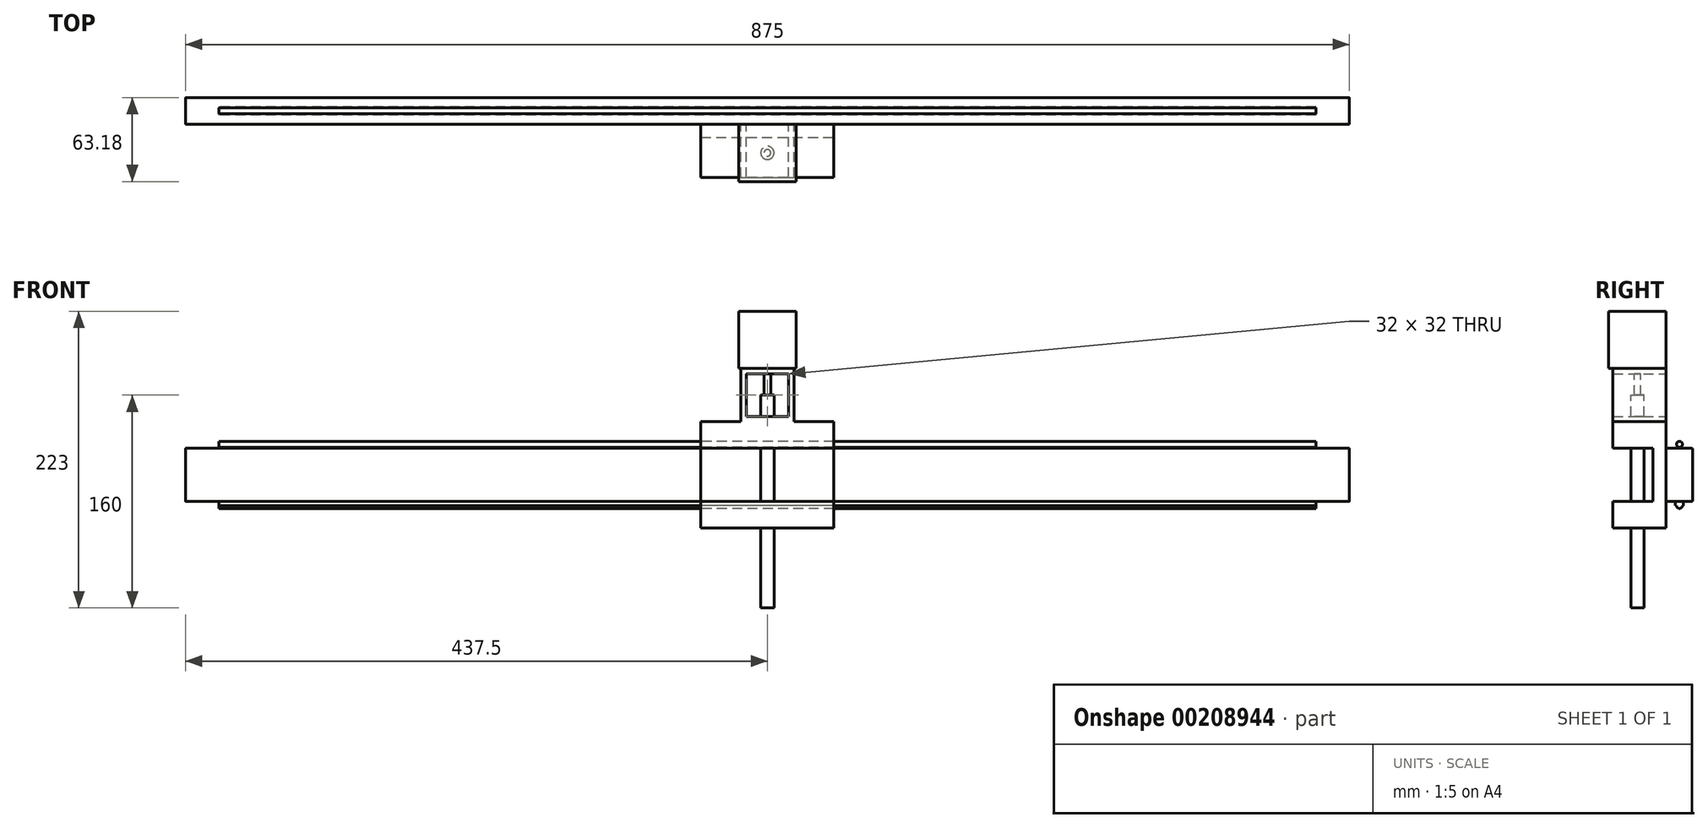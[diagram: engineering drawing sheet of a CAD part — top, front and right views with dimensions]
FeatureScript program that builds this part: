
annotation { "Feature Type Name" : "Feature", "Feature Type Description" : "" }
export const myFeature = defineFeature(function(context is Context, id is Id, definition is map)
    precondition{}
    {
        {
            var Q0;
            Q0=qCreatedBy(makeId("Right.planeOp"),FACE);
            var sketch = newSketch(context, id + "F0", { "sketchPlane" : qUnion([Q0])});
            skLineSegment(sketch, "E0.rect.bottom", {"start": v(-9, 20) * mm, "end": v(9, 20) * mm});
            skLineSegment(sketch, "E0.rect.top", {"start": v(-9, -20) * mm, "end": v(9, -20) * mm});
            skLineSegment(sketch, "E0.rect.left", {"start": v(-10, 19) * mm, "end": v(-10, -19) * mm});
            skLineSegment(sketch, "E0.rect.right", {"start": v(10, 19) * mm, "end": v(10, -19) * mm});
            skPoint(sketch, "E0.rect.middle", {"position": v(0, 0) * mm});
            skLineSegment(sketch, "E1.rect.bottom", {"start": v(3, 20) * mm, "end": v(-3, 20) * mm});
            skLineSegment(sketch, "E1.rect.top", {"start": v(3, 23) * mm, "end": v(-3, 23) * mm});
            skLineSegment(sketch, "E1.rect.left", {"start": v(3, 20) * mm, "end": v(3, 23) * mm});
            skLineSegment(sketch, "E1.rect.right", {"start": v(-3, 20) * mm, "end": v(-3, 23) * mm});
            skPoint(sketch, "E1.rect.middle", {"position": v(0, 21.5) * mm});
            skCircle(sketch, "E2", {"center": v(0, 23) * mm, "radius": 2.22 * mm});
            skPoint(sketch, "E3.MirrorP", {"position": v(0, -21.5) * mm});
            skLineSegment(sketch, "E4.MirrorCS", {"start": v(3, -23) * mm, "end": v(-3, -23) * mm});
            skCircle(sketch, "E5.MirrorC", {"center": v(0, -23) * mm, "radius": 2.22 * mm});
            skLineSegment(sketch, "E6.MirrorCS", {"start": v(3, -20) * mm, "end": v(3, -23) * mm});
            skLineSegment(sketch, "E7.MirrorCS", {"start": v(-3, -20) * mm, "end": v(-3, -23) * mm});
            skPoint(sketch, "E8.visualSharp", {"position": v(10, 20) * mm});
            skArc(sketch, "E8.filletArc", {"start": v(10, 19) * mm, "mid": v(9.7, 19.7) * mm, "end": v(9, 20) * mm});
            skPoint(sketch, "E9.visualSharp", {"position": v(-10, 20) * mm});
            skArc(sketch, "E9.filletArc", {"start": v(-9, 20) * mm, "mid": v(-9.7, 19.7) * mm, "end": v(-10, 19) * mm});
            skPoint(sketch, "E10.visualSharp", {"position": v(-10, -20) * mm});
            skArc(sketch, "E10.filletArc", {"start": v(-10, -19) * mm, "mid": v(-9.7, -19.7) * mm, "end": v(-9, -20) * mm});
            skPoint(sketch, "E11.visualSharp", {"position": v(10, -20) * mm});
            skArc(sketch, "E11.filletArc", {"start": v(9, -20) * mm, "mid": v(9.7, -19.7) * mm, "end": v(10, -19) * mm});
            skSolve(sketch);
        }
        {
            var Q0;
            Q0=qCreatedBy(makeId("Right.planeOp"),FACE);
            var sketch = newSketch(context, id + "F1", { "sketchPlane" : qUnion([Q0])});
            skPoint(sketch, "E12.rect.middle", {"position": v(15, 0) * mm});
            skLineSegment(sketch, "E13.MirrorCS", {"start": v(-10, -40) * mm, "end": v(-20, -40) * mm});
            skLineSegment(sketch, "E14.MirrorCS", {"start": v(-10, 40) * mm, "end": v(-20, 40) * mm});
            skPoint(sketch, "E15.MirrorP", {"position": v(-15, 0) * mm});
            skLineSegment(sketch, "E16.MirrorCS", {"start": v(-20, 40) * mm, "end": v(-20, -40) * mm});
            skLineSegment(sketch, "E17.MirrorCS", {"start": v(-10, 40) * mm, "end": v(-10, -40) * mm});
            skSolve(sketch);
        }
        {
            var Q0;
            {var subQ3=sQuery(id+"F0.wireOp",EDGE,"E0.rect.left");Q0=makeQuery(id+"F0.imprint","IMPRINT",FACE,{"disambiguationData":[TD([[makeQuery(id+"F0.imprint","IMPRINT",EDGE,{"derivedFrom":subQ3}),1.0]])]});}
            extrude(context, id + "F2", {"entities" : qUnion([Q0]), "endBound" : BoundingType.SYMMETRIC, "oppositeDirection" : true, "depth" : 875 * mm});
        }
        {
            var Q0;
            {var subQ0=sQuery(id+"F0.wireOp",EDGE,"E2");var subQ1=sQuery(id+"F0.wireOp",EDGE,"E1.rect.top");var subQ2=makeQuery(id+"F0.imprint","INTERSECT",VERTEX,{"disambiguationData":[OD(0.0)],"derivedFrom":[subQ1,subQ0]});Q0=makeQuery(id+"F0.imprint","IMPRINT",FACE,{"disambiguationData":[TD([[makeQuery(id+"F0.imprint","IMPRINT",EDGE,{"disambiguationData":[TD([[subQ2,-1.0]])],"derivedFrom":subQ1}),-1.0]])]});}
            var Q1;
            {var subQ0=sQuery(id+"F0.wireOp",EDGE,"E2");var subQ1=sQuery(id+"F0.wireOp",EDGE,"E1.rect.top");var subQ2=makeQuery(id+"F0.imprint","INTERSECT",VERTEX,{"disambiguationData":[OD(0.0)],"derivedFrom":[subQ1,subQ0]});Q1=makeQuery(id+"F0.imprint","IMPRINT",FACE,{"disambiguationData":[TD([[makeQuery(id+"F0.imprint","IMPRINT",EDGE,{"disambiguationData":[TD([[subQ2,-1.0]])],"derivedFrom":subQ1}),1.0]])]});}
            var Q2;
            Q2=makeQuery(id+"F0.imprint","IMPRINT",FACE,{"disambiguationData":[TD([[makeQuery(id+"F0.imprint","IMPRINT",EDGE,{"derivedFrom":sQuery(id+"F0.wireOp",EDGE,"E1.rect.bottom")}),-1.0]])]});
            var Q3;
            {var subQ0=sQuery(id+"F0.wireOp",EDGE,"E5.MirrorC");var subQ1=sQuery(id+"F0.wireOp",EDGE,"E4.MirrorCS");var subQ2=makeQuery(id+"F0.imprint","INTERSECT",VERTEX,{"disambiguationData":[OD(0.0)],"derivedFrom":[subQ1,subQ0]});Q3=makeQuery(id+"F0.imprint","IMPRINT",FACE,{"disambiguationData":[TD([[makeQuery(id+"F0.imprint","IMPRINT",EDGE,{"disambiguationData":[TD([[subQ2,-1.0]])],"derivedFrom":subQ1}),1.0]])]});}
            var Q4;
            {var subQ4=sQuery(id+"F0.wireOp",EDGE,"E6.MirrorCS");Q4=makeQuery(id+"F0.imprint","IMPRINT",FACE,{"disambiguationData":[TD([[makeQuery(id+"F0.imprint","IMPRINT",EDGE,{"derivedFrom":subQ4}),-1.0]])]});}
            var Q5;
            {var subQ0=sQuery(id+"F0.wireOp",EDGE,"E5.MirrorC");var subQ1=sQuery(id+"F0.wireOp",EDGE,"E4.MirrorCS");var subQ2=makeQuery(id+"F0.imprint","INTERSECT",VERTEX,{"disambiguationData":[OD(0.0)],"derivedFrom":[subQ1,subQ0]});Q5=makeQuery(id+"F0.imprint","IMPRINT",FACE,{"disambiguationData":[TD([[makeQuery(id+"F0.imprint","IMPRINT",EDGE,{"disambiguationData":[TD([[subQ2,-1.0]])],"derivedFrom":subQ1}),-1.0]])]});}
            extrude(context, id + "F3", {"entities" : qUnion([Q0, Q1, Q2, Q3, Q4, Q5]), "endBound" : BoundingType.SYMMETRIC, "depth" : 825 * mm});
        }
        {
            var Q0;
            Q0=makeQuery(id+"F1.imprint","IMPRINT",FACE,{"disambiguationData":[TD([[makeQuery(id+"F1.imprint","IMPRINT",EDGE,{"derivedFrom":sQuery(id+"F1.wireOp",EDGE,"E13.MirrorCS")}),-1.0]])]});
            extrude(context, id + "F4", {"entities" : qUnion([Q0]), "endBound" : BoundingType.SYMMETRIC, "depth" : 100 * mm});
        }
        {
            var Q0;
            Q0=makeQuery(id+"F4.opExtrude","SWEPT_FACE",FACE,{"disambiguationData":[OSD([sQuery(id+"F1.wireOp",EDGE,"E17.MirrorCS")])]});
            var sketch = newSketch(context, id + "F5", { "sketchPlane" : qUnion([Q0])});
            skLineSegment(sketch, "E18.rect.bottom", {"start": v(20, 40) * mm, "end": v(-20, 40) * mm});
            skLineSegment(sketch, "E18.rect.top", {"start": v(20, 80) * mm, "end": v(-20, 80) * mm});
            skLineSegment(sketch, "E18.rect.left", {"start": v(20, 40) * mm, "end": v(20, 80) * mm});
            skLineSegment(sketch, "E18.rect.right", {"start": v(-20, 40) * mm, "end": v(-20, 80) * mm});
            skPoint(sketch, "E18.rect.middle", {"position": v(0, 60) * mm});
            skPoint(sketch, "E18.rect.middle.positionSnap0", {"position": v(0, 40) * mm});
            skPoint(sketch, "E18.rect.centerSnap0", {"position": v(0, 40) * mm});
            skLineSegment(sketch, "E19.rect.bottom", {"start": v(16, 76) * mm, "end": v(-16, 76) * mm});
            skLineSegment(sketch, "E19.rect.top", {"start": v(16, 44) * mm, "end": v(-16, 44) * mm});
            skLineSegment(sketch, "E19.rect.left", {"start": v(16, 76) * mm, "end": v(16, 44) * mm});
            skLineSegment(sketch, "E19.rect.right", {"start": v(-16, 76) * mm, "end": v(-16, 44) * mm});
            skPoint(sketch, "E20", {"position": v(0, 52.71) * mm});
            skPoint(sketch, "E20.positionSnap0", {"position": v(0, 44) * mm});
            skSolve(sketch);
        }
        {
            var Q0;
            Q0=makeQuery(id+"F5.imprint","IMPRINT",FACE,{"disambiguationData":[TD([[makeQuery(id+"F5.imprint","IMPRINT",EDGE,{"derivedFrom":sQuery(id+"F5.wireOp",EDGE,"E18.rect.bottom")}),1.0]])]});
            extrude(context, id + "F6", {"entities" : qUnion([Q0]), "oppositeDirection" : true, "depth" : 40 * mm});
        }
        {
            var Q0;
            Q0=makeQuery(id+"F6.opExtrude","SWEPT_FACE",FACE,{"disambiguationData":[OSD([sQuery(id+"F5.wireOp",EDGE,"E18.rect.top")])]});
            var sketch = newSketch(context, id + "F7", { "sketchPlane" : qUnion([Q0])});
            skLineSegment(sketch, "E21.rect.bottom", {"start": v(21.59, -10) * mm, "end": v(-21.59, -10) * mm});
            skLineSegment(sketch, "E21.rect.top", {"start": v(21.59, -53.18) * mm, "end": v(-21.6, -53.18) * mm});
            skLineSegment(sketch, "E21.rect.left", {"start": v(21.59, -10) * mm, "end": v(21.59, -53.18) * mm});
            skLineSegment(sketch, "E21.rect.right", {"start": v(-21.6, -10) * mm, "end": v(-21.6, -53.18) * mm});
            skPoint(sketch, "E21.rect.middle", {"position": v(0, -31.6) * mm});
            skPoint(sketch, "E21.rect.middle.positionSnap0", {"position": v(0, -20) * mm});
            skPoint(sketch, "E21.rect.centerSnap0", {"position": v(0, -20) * mm});
            skCircle(sketch, "E22", {"center": v(0, -31.6) * mm, "radius": 2.5 * mm});
            skSolve(sketch);
        }
        {
            var Q0;
            Q0=qCreatedBy(makeId("Top.planeOp"),FACE);
            var sketch = newSketch(context, id + "F8", { "sketchPlane" : qUnion([Q0])});
            skCircle(sketch, "E23", {"center": v(0, -31.59) * mm, "radius": 5 * mm});
            skSolve(sketch);
        }
        {
            var Q0;
            Q0=makeQuery(id+"F8.imprint","IMPRINT",FACE,{"disambiguationData":[TD([[makeQuery(id+"F8.imprint","IMPRINT",EDGE,{"derivedFrom":sQuery(id+"F8.wireOp",EDGE,"E23")}),1.0]])]});
            extrude(context, id + "F9", {"entities" : qUnion([Q0]), "oppositeDirection" : true, "depth" : 100 * mm, "hasSecondDirection" : true, "secondDirectionOppositeDirection" : false, "secondDirectionDepth" : 60 * mm});
        }
        {
            var Q0;
            Q0=qSketchRegion(id+"F7",true);
            var Q1;
            Q1=makeQuery(id+"F7.imprint","IMPRINT",FACE,{"disambiguationData":[TD([[makeQuery(id+"F7.imprint","IMPRINT",EDGE,{"derivedFrom":sQuery(id+"F7.wireOp",EDGE,"E22")}),1.0]])]});
            extrude(context, id + "F10", {"entities" : qUnion([Q0, Q1]), "depth" : 43 * mm});
        }
        {
            var Q0;
            Q0=makeQuery(id+"F7.imprint","IMPRINT",FACE,{"disambiguationData":[TD([[makeQuery(id+"F7.imprint","IMPRINT",EDGE,{"derivedFrom":sQuery(id+"F7.wireOp",EDGE,"E22")}),1.0]])]});
            extrude(context, id + "F11", {"entities" : qUnion([Q0]), "operationType" : NewBodyOperationType.ADD, "oppositeDirection" : true, "depth" : 20 * mm});
        }
        {
            var Q0;
            Q0=makeQuery(id+"F4.opExtrude","SWEPT_FACE",FACE,{"disambiguationData":[OSD([sQuery(id+"F1.wireOp",EDGE,"E16.MirrorCS")])]});
            var sketch = newSketch(context, id + "F12", { "sketchPlane" : qUnion([Q0])});
            skLineSegment(sketch, "E24.bottom", {"start": v(-50, 40) * mm, "end": v(50, 40) * mm});
            skLineSegment(sketch, "E24.top", {"start": v(-50, 20) * mm, "end": v(50, 20) * mm});
            skLineSegment(sketch, "E24.left", {"start": v(-50, 40) * mm, "end": v(-50, 20) * mm});
            skLineSegment(sketch, "E24.right", {"start": v(50, 40) * mm, "end": v(50, 20) * mm});
            skLineSegment(sketch, "E25.bottom", {"start": v(-50, -40) * mm, "end": v(50, -40) * mm});
            skLineSegment(sketch, "E25.top", {"start": v(-50, -20) * mm, "end": v(50, -20) * mm});
            skLineSegment(sketch, "E25.left", {"start": v(-50, -40) * mm, "end": v(-50, -20) * mm});
            skLineSegment(sketch, "E25.right", {"start": v(50, -40) * mm, "end": v(50, -20) * mm});
            skSolve(sketch);
        }
        {
            var Q0;
            Q0=makeQuery(id+"F12.imprint","IMPRINT",FACE,{"disambiguationData":[TD([[makeQuery(id+"F12.imprint","IMPRINT",EDGE,{"derivedFrom":sQuery(id+"F12.wireOp",EDGE,"E24.bottom")}),1.0]])]});
            var Q1;
            Q1=makeQuery(id+"F12.imprint","IMPRINT",FACE,{"disambiguationData":[TD([[makeQuery(id+"F12.imprint","IMPRINT",EDGE,{"derivedFrom":sQuery(id+"F12.wireOp",EDGE,"E25.bottom")}),-1.0]])]});
            extrude(context, id + "F13", {"entities" : qUnion([Q0, Q1]), "operationType" : NewBodyOperationType.ADD, "depth" : 30 * mm});
        }
    });
